# Revit family: F-05BT_WT v1.1
name_source: partatom
category: 通信装置
units: mm (PartAtom-declared; Revit-internal decimal feet)

## family parameters
パーツ タイプ = 標準
ロード時にボイドで切り取り = いいえ
丸型コネクタ寸法 = 直径を使用
作業面ベース = いいえ
共有 = いいえ
常に垂直 = はい
注釈の向きを維持 = いいえ
部屋計算ポイント = いいえ

## types (2) — shared parameters
Accessory = Speaker bracket x1,  Base  bracket  x1,  Base  bracket  cover  x1,  Bracket  fixinq  screw  x1  set
Crossover Frequency = 4.5kHz
Depth = 164  [stored 0.538058 ft]
Dimensions = 162(W) × 274(H) ×164(D)mm (6.28" x 10.79" x 6.46")
Directivty Angle = Horizontal: 100', Vertical: 100’
Frequency Response = 60Hz~20kHz - 10dB  at installation in 1/2 free sound field
Height = 274  [stored 0.89895 ft]
Input Terminal = Push-in terminal
Instollation Environment = Indoor installation
Operoting Temperature = -10°C~+50°C
Option - Speaker Stando = ST-34B  Note:  KAM 19780  or  KAM 19610  is  required.
Power Handling Capacity = Rated noise power: 60 W (8Ω), Continuous program: 120 W (8Ω)
Product Info = https://www.toa-products.com
Rated Impedance (100V line) = 330Ω (30W), 1kΩ (10W), 3.3kΩ (3W), 10kΩ (1W)
Rated Impedance (70V line) = 170Ω (30W), 330Ω (15W), 1kΩ (5W), 3.3kΩ (1.5W), 10kΩ (0.5W)
Rated Impedance (Low) = 8Ω
Rated Input = 30 W (100 V line, 70 V line)
Sensitivty = 90dB (1W, 1m)  at installation in 1/2 free sound field
Speaker Component - High frequency = 25mm (1") Dome Tweeter
Speaker Component - Low frequency = 13cm (5") PP cone type
URL = https://www.toa.jp
Update Info = https://www.sound-toa.com
Version = 1
Weight = 2.7kg (5.95 lb)
Width = 162  [stored 0.531496 ft]
製造元 = TOA
zero-valued in all types: 既定の高さ

## per-type parameters (varying)
| type | Body | Enclosure | Finish - Base bracket | Finish - Base bracket cover | Finish - Enclosure | Finish - Grille | Finish - Speaker bracket | Grille | Oprion - Adapter plate | モデル |
| F-05BT (Black) | TOA-Body(Black) | Bass-reflex type | Steel  plate,  t4,  black  (RAL  9011  equivalent),  paint | HIPS,  black (RAL  9011  equivalent) | HIPS,  block (RAL 9011 equivalent),  paint | Aluminum,  black  (RAL  9011  equivalent),  paint | Die-cast  aluminum,  block (RAL  9011  equivalent), paint | TOA-Grille(Black) | HY-F05B | F-05BT |
| F-05WT (White) | TOA-Body(White) | Bass-reflex type
Bass—reflex   type
Bass—reflex   type | Steel  plate,  t4,  white  (RAL  9016  equivalent),  paint | HIPS,  white (RAL  9016  equivalent) | HIPS,  white (RAL  9016 equivalent),  paint | Aluminum,  white  (RAL  9016  equivalent),  paint | Die-cast  aluminum,  white (RAL  9016  equivalent), paint | TOA-Grille(White) | HY-F05W | F-05WT |

note: [stored X ft] marks values corroborated as IEEE doubles in the binary element streams (Revit-internal decimal feet)
